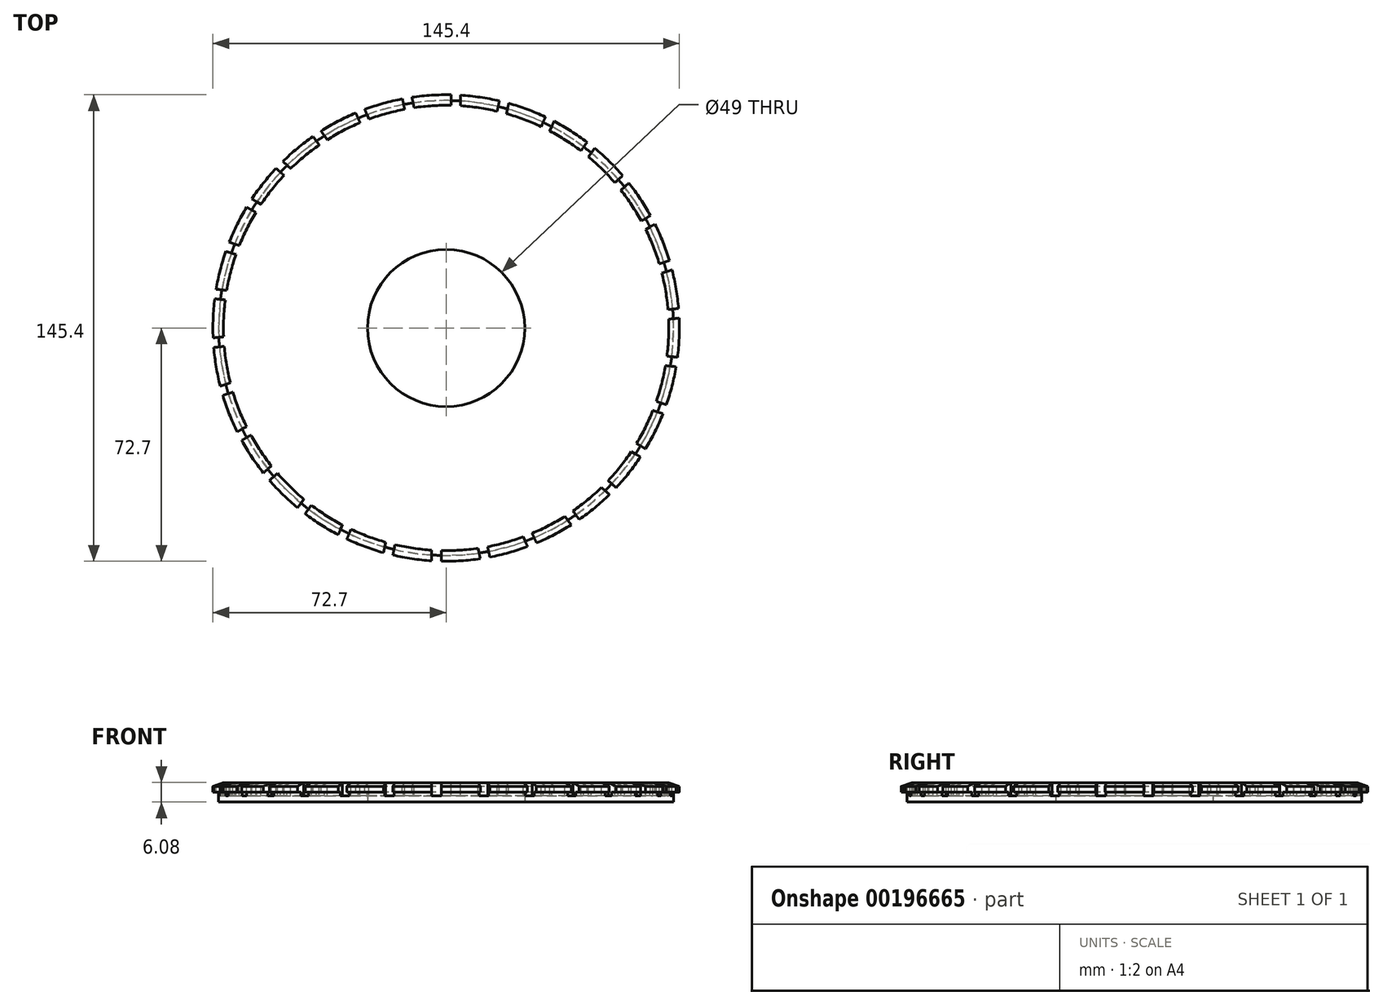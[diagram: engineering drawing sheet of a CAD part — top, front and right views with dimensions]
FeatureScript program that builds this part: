
annotation { "Feature Type Name" : "Feature", "Feature Type Description" : "" }
export const myFeature = defineFeature(function(context is Context, id is Id, definition is map)
    precondition{}
    {
        {
            var Q0;
            Q0=qCreatedBy(makeId("Right.planeOp"),FACE);
            var sketch = newSketch(context, id + "F0", { "sketchPlane" : qUnion([Q0])});
            skLineSegment(sketch, "E0", {"start": v(0, 85.68) * mm, "end": v(0, -86.46) * mm, "construction": true});
            skLineSegment(sketch, "E1.bottom", {"start": v(0, 0) * mm, "end": v(70.9, 0) * mm});
            skLineSegment(sketch, "E1.top", {"start": v(0, 2) * mm, "end": v(69.4, 2) * mm});
            skLineSegment(sketch, "E1.left", {"start": v(0, 0) * mm, "end": v(0, 2) * mm});
            skLineSegment(sketch, "E1.right", {"start": v(70.9, 0) * mm, "end": v(70.9, 2) * mm});
            skLineSegment(sketch, "E2.bottom", {"start": v(70.9, 0) * mm, "end": v(69.4, 0) * mm});
            skLineSegment(sketch, "E2.left", {"start": v(70.9, 0) * mm, "end": v(70.9, 3.1) * mm});
            skLineSegment(sketch, "E3.top", {"start": v(70.9, 3.1) * mm, "end": v(72.7, 3.1) * mm});
            skLineSegment(sketch, "E4", {"start": v(72.7, 3.1) * mm, "end": v(72.7, 4.9) * mm});
            skLineSegment(sketch, "E5", {"start": v(72.7, 4.9) * mm, "end": v(69.4, 6.08) * mm});
            skLineSegment(sketch, "E6", {"start": v(69.4, 2) * mm, "end": v(69.4, 6.08) * mm});
            skSolve(sketch);
        }
        {
            var Q0;
            Q0 = qSketchRegion(id + "F0", true);
            var Q1;
            Q1=sQuery(id+"F0.wireOp",EDGE,"E0");
            revolve(context, id + "F1", {"entities" : qUnion([Q0]), "axis" : qUnion([Q1]), "revolveType" : RevolveType.FULL});
        }
        {
            var Q0;
            Q0=qCreatedBy(makeId("Top.planeOp"),FACE);
            var sketch = newSketch(context, id + "F2", { "sketchPlane" : qUnion([Q0])});
            skPoint(sketch, "E7", {"position": v(0, 0) * mm});
            skSolve(sketch);
        }
        {
            var Q0;
            Q0=sQuery(id+"F2.wireOp",VERTEX,"E7");
            var Q1;
            Q1=makeQuery(id+"F1.opRevolve","SWEPT_BODY",BODY,{"disambiguationData":[OSD([sQuery(id+"F0.wireOp",EDGE,"E1.bottom"),sQuery(id+"F0.wireOp",EDGE,"E1.top"),sQuery(id+"F0.wireOp",EDGE,"E1.left"),sQuery(id+"F0.wireOp",EDGE,"E2.bottom"),sQuery(id+"F0.wireOp",EDGE,"E2.top"),sQuery(id+"F0.wireOp",EDGE,"E2.left"),sQuery(id+"F0.wireOp",EDGE,"E2.right"),sQuery(id+"F0.wireOp",EDGE,"E3.top"),sQuery(id+"F0.wireOp",EDGE,"KGbcwsE4-q3BG-QgxK-r2mv-6eEFrDaZc8Cp"),sQuery(id+"F0.wireOp",EDGE,"3cbed7ed-6242-46d1-abfa-7344cad13317.trimOffspring")])]});
            hole(context, id + "F3", {"style" : HoleStyle.SIMPLE, "endStyle" : HoleEndStyle.BLIND, "oppositeDirection" : true, "holeDiameter" : 49 * mm, "holeDepth" : 100 * mm, "startFromSketch" : true, "locations" : qUnion([Q0]), "scope" : qUnion([Q1])});
        }
        {
            var Q0;
            Q0=makeQuery(id+"F1.opRevolve","SWEPT_FACE",FACE,{"disambiguationData":[OSD([sQuery(id+"F0.wireOp",EDGE,"E1.top")])]});
            var sketch = newSketch(context, id + "F4", { "sketchPlane" : qUnion([Q0])});
            skLineSegment(sketch, "E8.bottom", {"start": v(-4.53, -77.52) * mm, "end": v(-1.53, -77.52) * mm});
            skLineSegment(sketch, "E8.top", {"start": v(-4.53, -61.97) * mm, "end": v(-1.53, -61.97) * mm});
            skLineSegment(sketch, "E8.left", {"start": v(-4.53, -77.52) * mm, "end": v(-4.53, -61.97) * mm});
            skLineSegment(sketch, "E8.right", {"start": v(-1.53, -77.52) * mm, "end": v(-1.53, -61.97) * mm});
            skLineSegment(sketch, "E9.1.0", {"start": v(11.7, -76.77) * mm, "end": v(8.46, -61.56) * mm});
            skLineSegment(sketch, "E9.1.1", {"start": v(14.63, -76.15) * mm, "end": v(11.4, -60.94) * mm});
            skLineSegment(sketch, "E9.1.2", {"start": v(11.7, -76.77) * mm, "end": v(14.63, -76.15) * mm});
            skLineSegment(sketch, "E9.1.3", {"start": v(8.46, -61.56) * mm, "end": v(11.4, -60.94) * mm});
            skLineSegment(sketch, "E9.2.0", {"start": v(27.4, -72.66) * mm, "end": v(21.07, -58.46) * mm});
            skLineSegment(sketch, "E9.2.1", {"start": v(30.14, -71.44) * mm, "end": v(23.81, -57.24) * mm});
            skLineSegment(sketch, "E9.2.2", {"start": v(27.4, -72.66) * mm, "end": v(30.14, -71.44) * mm});
            skLineSegment(sketch, "E9.2.3", {"start": v(21.07, -58.46) * mm, "end": v(23.81, -57.24) * mm});
            skLineSegment(sketch, "E9.3.0", {"start": v(41.9, -65.38) * mm, "end": v(32.77, -52.8) * mm});
            skLineSegment(sketch, "E9.3.1", {"start": v(44.33, -63.62) * mm, "end": v(35.2, -51.03) * mm});
            skLineSegment(sketch, "E9.3.2", {"start": v(41.9, -65.38) * mm, "end": v(44.33, -63.62) * mm});
            skLineSegment(sketch, "E9.3.3", {"start": v(32.77, -52.8) * mm, "end": v(35.2, -51.03) * mm});
            skLineSegment(sketch, "E9.4.0", {"start": v(54.58, -55.24) * mm, "end": v(43.03, -44.83) * mm});
            skLineSegment(sketch, "E9.4.1", {"start": v(56.6, -53) * mm, "end": v(45.03, -42.6) * mm});
            skLineSegment(sketch, "E9.4.2", {"start": v(54.58, -55.24) * mm, "end": v(56.6, -53) * mm});
            skLineSegment(sketch, "E9.4.3", {"start": v(43.03, -44.83) * mm, "end": v(45.03, -42.6) * mm});
            skLineSegment(sketch, "E9.5.0", {"start": v(64.87, -42.68) * mm, "end": v(51.4, -34.9) * mm});
            skLineSegment(sketch, "E9.5.1", {"start": v(66.37, -40.08) * mm, "end": v(52.9, -32.3) * mm});
            skLineSegment(sketch, "E9.5.2", {"start": v(64.87, -42.68) * mm, "end": v(66.37, -40.08) * mm});
            skLineSegment(sketch, "E9.5.3", {"start": v(51.4, -34.9) * mm, "end": v(52.9, -32.3) * mm});
            skLineSegment(sketch, "E9.6.0", {"start": v(72.33, -28.26) * mm, "end": v(57.54, -23.46) * mm});
            skLineSegment(sketch, "E9.6.1", {"start": v(73.26, -25.4) * mm, "end": v(58.47, -20.6) * mm});
            skLineSegment(sketch, "E9.6.2", {"start": v(72.33, -28.26) * mm, "end": v(73.26, -25.4) * mm});
            skLineSegment(sketch, "E9.6.3", {"start": v(57.54, -23.46) * mm, "end": v(58.47, -20.6) * mm});
            skLineSegment(sketch, "E9.7.0", {"start": v(76.63, -12.6) * mm, "end": v(61.16, -10.98) * mm});
            skLineSegment(sketch, "E9.7.1", {"start": v(76.94, -9.62) * mm, "end": v(61.47, -8) * mm});
            skLineSegment(sketch, "E9.7.2", {"start": v(76.63, -12.6) * mm, "end": v(76.94, -9.62) * mm});
            skLineSegment(sketch, "E9.7.3", {"start": v(61.16, -10.98) * mm, "end": v(61.47, -8) * mm});
            skLineSegment(sketch, "E9.8.0", {"start": v(77.57, 3.6) * mm, "end": v(62.1, 1.98) * mm});
            skLineSegment(sketch, "E9.8.1", {"start": v(77.26, 6.59) * mm, "end": v(61.8, 4.96) * mm});
            skLineSegment(sketch, "E9.8.2", {"start": v(77.57, 3.6) * mm, "end": v(77.26, 6.59) * mm});
            skLineSegment(sketch, "E9.8.3", {"start": v(62.1, 1.98) * mm, "end": v(61.8, 4.96) * mm});
            skLineSegment(sketch, "E9.9.0", {"start": v(75.13, 19.65) * mm, "end": v(60.34, 14.85) * mm});
            skLineSegment(sketch, "E9.9.1", {"start": v(74.2, 22.5) * mm, "end": v(59.41, 17.7) * mm});
            skLineSegment(sketch, "E9.9.2", {"start": v(75.13, 19.65) * mm, "end": v(74.2, 22.5) * mm});
            skLineSegment(sketch, "E9.9.3", {"start": v(60.34, 14.85) * mm, "end": v(59.41, 17.7) * mm});
            skLineSegment(sketch, "E9.10.0", {"start": v(69.4, 34.84) * mm, "end": v(55.93, 27.07) * mm});
            skLineSegment(sketch, "E9.10.1", {"start": v(67.9, 37.44) * mm, "end": v(54.43, 29.66) * mm});
            skLineSegment(sketch, "E9.10.2", {"start": v(69.4, 34.84) * mm, "end": v(67.9, 37.44) * mm});
            skLineSegment(sketch, "E9.10.3", {"start": v(55.93, 27.07) * mm, "end": v(54.43, 29.66) * mm});
            skLineSegment(sketch, "E9.11.0", {"start": v(60.64, 48.51) * mm, "end": v(49.08, 38.1) * mm});
            skLineSegment(sketch, "E9.11.1", {"start": v(58.63, 50.74) * mm, "end": v(47.08, 40.33) * mm});
            skLineSegment(sketch, "E9.11.2", {"start": v(60.64, 48.51) * mm, "end": v(58.63, 50.74) * mm});
            skLineSegment(sketch, "E9.11.3", {"start": v(49.08, 38.1) * mm, "end": v(47.08, 40.33) * mm});
            skLineSegment(sketch, "E9.12.0", {"start": v(49.23, 60.06) * mm, "end": v(40.09, 47.48) * mm});
            skLineSegment(sketch, "E9.12.1", {"start": v(46.8, 61.82) * mm, "end": v(37.66, 49.24) * mm});
            skLineSegment(sketch, "E9.12.2", {"start": v(49.23, 60.06) * mm, "end": v(46.8, 61.82) * mm});
            skLineSegment(sketch, "E9.12.3", {"start": v(40.09, 47.48) * mm, "end": v(37.66, 49.24) * mm});
            skLineSegment(sketch, "E9.13.0", {"start": v(35.67, 68.98) * mm, "end": v(29.34, 54.77) * mm});
            skLineSegment(sketch, "E9.13.1", {"start": v(32.93, 70.2) * mm, "end": v(26.6, 56) * mm});
            skLineSegment(sketch, "E9.13.2", {"start": v(35.67, 68.98) * mm, "end": v(32.93, 70.2) * mm});
            skLineSegment(sketch, "E9.13.3", {"start": v(29.34, 54.77) * mm, "end": v(26.6, 56) * mm});
            skLineSegment(sketch, "E9.14.0", {"start": v(20.55, 74.89) * mm, "end": v(17.31, 59.68) * mm});
            skLineSegment(sketch, "E9.14.1", {"start": v(17.61, 75.51) * mm, "end": v(14.38, 60.3) * mm});
            skLineSegment(sketch, "E9.14.2", {"start": v(20.55, 74.89) * mm, "end": v(17.61, 75.51) * mm});
            skLineSegment(sketch, "E9.14.3", {"start": v(17.31, 59.68) * mm, "end": v(14.38, 60.3) * mm});
            skLineSegment(sketch, "E9.15.0", {"start": v(4.53, 77.52) * mm, "end": v(4.53, 61.97) * mm});
            skLineSegment(sketch, "E9.15.1", {"start": v(1.53, 77.52) * mm, "end": v(1.53, 61.97) * mm});
            skLineSegment(sketch, "E9.15.2", {"start": v(4.53, 77.52) * mm, "end": v(1.53, 77.52) * mm});
            skLineSegment(sketch, "E9.15.3", {"start": v(4.53, 61.97) * mm, "end": v(1.53, 61.97) * mm});
            skLineSegment(sketch, "E9.16.0", {"start": v(-11.7, 76.77) * mm, "end": v(-8.46, 61.56) * mm});
            skLineSegment(sketch, "E9.16.1", {"start": v(-14.63, 76.15) * mm, "end": v(-11.4, 60.94) * mm});
            skLineSegment(sketch, "E9.16.2", {"start": v(-11.7, 76.77) * mm, "end": v(-14.63, 76.15) * mm});
            skLineSegment(sketch, "E9.16.3", {"start": v(-8.46, 61.56) * mm, "end": v(-11.4, 60.94) * mm});
            skLineSegment(sketch, "E9.17.0", {"start": v(-27.4, 72.66) * mm, "end": v(-21.07, 58.46) * mm});
            skLineSegment(sketch, "E9.17.1", {"start": v(-30.14, 71.44) * mm, "end": v(-23.81, 57.24) * mm});
            skLineSegment(sketch, "E9.17.2", {"start": v(-27.4, 72.66) * mm, "end": v(-30.14, 71.44) * mm});
            skLineSegment(sketch, "E9.17.3", {"start": v(-21.07, 58.46) * mm, "end": v(-23.81, 57.24) * mm});
            skLineSegment(sketch, "E9.18.0", {"start": v(-41.9, 65.38) * mm, "end": v(-32.77, 52.8) * mm});
            skLineSegment(sketch, "E9.18.1", {"start": v(-44.33, 63.62) * mm, "end": v(-35.2, 51.03) * mm});
            skLineSegment(sketch, "E9.18.2", {"start": v(-41.9, 65.38) * mm, "end": v(-44.33, 63.62) * mm});
            skLineSegment(sketch, "E9.18.3", {"start": v(-32.77, 52.8) * mm, "end": v(-35.2, 51.03) * mm});
            skLineSegment(sketch, "E9.19.0", {"start": v(-54.58, 55.24) * mm, "end": v(-43.03, 44.83) * mm});
            skLineSegment(sketch, "E9.19.1", {"start": v(-56.6, 53) * mm, "end": v(-45.03, 42.6) * mm});
            skLineSegment(sketch, "E9.19.2", {"start": v(-54.58, 55.24) * mm, "end": v(-56.6, 53) * mm});
            skLineSegment(sketch, "E9.19.3", {"start": v(-43.03, 44.83) * mm, "end": v(-45.03, 42.6) * mm});
            skLineSegment(sketch, "E9.20.0", {"start": v(-64.87, 42.68) * mm, "end": v(-51.4, 34.9) * mm});
            skLineSegment(sketch, "E9.20.1", {"start": v(-66.37, 40.08) * mm, "end": v(-52.9, 32.3) * mm});
            skLineSegment(sketch, "E9.20.2", {"start": v(-64.87, 42.68) * mm, "end": v(-66.37, 40.08) * mm});
            skLineSegment(sketch, "E9.20.3", {"start": v(-51.4, 34.9) * mm, "end": v(-52.9, 32.3) * mm});
            skLineSegment(sketch, "E9.21.0", {"start": v(-72.33, 28.26) * mm, "end": v(-57.54, 23.46) * mm});
            skLineSegment(sketch, "E9.21.1", {"start": v(-73.26, 25.4) * mm, "end": v(-58.47, 20.6) * mm});
            skLineSegment(sketch, "E9.21.2", {"start": v(-72.33, 28.26) * mm, "end": v(-73.26, 25.4) * mm});
            skLineSegment(sketch, "E9.21.3", {"start": v(-57.54, 23.46) * mm, "end": v(-58.47, 20.6) * mm});
            skLineSegment(sketch, "E9.22.0", {"start": v(-76.63, 12.6) * mm, "end": v(-61.16, 10.98) * mm});
            skLineSegment(sketch, "E9.22.1", {"start": v(-76.94, 9.62) * mm, "end": v(-61.47, 8) * mm});
            skLineSegment(sketch, "E9.22.2", {"start": v(-76.63, 12.6) * mm, "end": v(-76.94, 9.62) * mm});
            skLineSegment(sketch, "E9.22.3", {"start": v(-61.16, 10.98) * mm, "end": v(-61.47, 8) * mm});
            skLineSegment(sketch, "E9.23.0", {"start": v(-77.57, -3.6) * mm, "end": v(-62.1, -1.98) * mm});
            skLineSegment(sketch, "E9.23.1", {"start": v(-77.26, -6.59) * mm, "end": v(-61.8, -4.96) * mm});
            skLineSegment(sketch, "E9.23.2", {"start": v(-77.57, -3.6) * mm, "end": v(-77.26, -6.59) * mm});
            skLineSegment(sketch, "E9.23.3", {"start": v(-62.1, -1.98) * mm, "end": v(-61.8, -4.96) * mm});
            skLineSegment(sketch, "E9.24.0", {"start": v(-75.13, -19.65) * mm, "end": v(-60.34, -14.85) * mm});
            skLineSegment(sketch, "E9.24.1", {"start": v(-74.2, -22.5) * mm, "end": v(-59.41, -17.7) * mm});
            skLineSegment(sketch, "E9.24.2", {"start": v(-75.13, -19.65) * mm, "end": v(-74.2, -22.5) * mm});
            skLineSegment(sketch, "E9.24.3", {"start": v(-60.34, -14.85) * mm, "end": v(-59.41, -17.7) * mm});
            skLineSegment(sketch, "E9.25.0", {"start": v(-69.4, -34.84) * mm, "end": v(-55.93, -27.07) * mm});
            skLineSegment(sketch, "E9.25.1", {"start": v(-67.9, -37.44) * mm, "end": v(-54.43, -29.66) * mm});
            skLineSegment(sketch, "E9.25.2", {"start": v(-69.4, -34.84) * mm, "end": v(-67.9, -37.44) * mm});
            skLineSegment(sketch, "E9.25.3", {"start": v(-55.93, -27.07) * mm, "end": v(-54.43, -29.66) * mm});
            skLineSegment(sketch, "E9.26.0", {"start": v(-60.64, -48.51) * mm, "end": v(-49.08, -38.1) * mm});
            skLineSegment(sketch, "E9.26.1", {"start": v(-58.63, -50.74) * mm, "end": v(-47.08, -40.33) * mm});
            skLineSegment(sketch, "E9.26.2", {"start": v(-60.64, -48.51) * mm, "end": v(-58.63, -50.74) * mm});
            skLineSegment(sketch, "E9.26.3", {"start": v(-49.08, -38.1) * mm, "end": v(-47.08, -40.33) * mm});
            skLineSegment(sketch, "E9.27.0", {"start": v(-49.23, -60.06) * mm, "end": v(-40.09, -47.48) * mm});
            skLineSegment(sketch, "E9.27.1", {"start": v(-46.8, -61.82) * mm, "end": v(-37.66, -49.24) * mm});
            skLineSegment(sketch, "E9.27.2", {"start": v(-49.23, -60.06) * mm, "end": v(-46.8, -61.82) * mm});
            skLineSegment(sketch, "E9.27.3", {"start": v(-40.09, -47.48) * mm, "end": v(-37.66, -49.24) * mm});
            skLineSegment(sketch, "E9.28.0", {"start": v(-35.67, -68.98) * mm, "end": v(-29.34, -54.77) * mm});
            skLineSegment(sketch, "E9.28.1", {"start": v(-32.93, -70.2) * mm, "end": v(-26.6, -56) * mm});
            skLineSegment(sketch, "E9.28.2", {"start": v(-35.67, -68.98) * mm, "end": v(-32.93, -70.2) * mm});
            skLineSegment(sketch, "E9.28.3", {"start": v(-29.34, -54.77) * mm, "end": v(-26.6, -56) * mm});
            skLineSegment(sketch, "E9.29.0", {"start": v(-20.55, -74.89) * mm, "end": v(-17.31, -59.68) * mm});
            skLineSegment(sketch, "E9.29.1", {"start": v(-17.61, -75.51) * mm, "end": v(-14.38, -60.3) * mm});
            skLineSegment(sketch, "E9.29.2", {"start": v(-20.55, -74.89) * mm, "end": v(-17.61, -75.51) * mm});
            skLineSegment(sketch, "E9.29.3", {"start": v(-17.31, -59.68) * mm, "end": v(-14.38, -60.3) * mm});
            skPoint(sketch, "E9.center", {"position": v(0, 0) * mm});
            skSolve(sketch);
        }
        {
            var Q0;
            Q0 = qSketchRegion(id + "F4", true);
            extrude(context, id + "F5", {"entities" : qUnion([Q0]), "operationType" : NewBodyOperationType.REMOVE, "depth" : 25 * mm});
        }
    });
